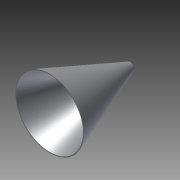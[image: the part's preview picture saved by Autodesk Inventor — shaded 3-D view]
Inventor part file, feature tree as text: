
AUTODESK INVENTOR PART (.ipt)
format: ipt  version: 2012 (Build 160160000, 160)  size: 94,208 bytes
history: native  units: in
note: dims shown in document units (in); Inventor stores cm internally (conversion verified against a paired STEP export)
features: sketch x2, plane x2, loft x1, shell x1
ambient origin geometry x8: Origin, YZ Plane, XZ Plane, XY Plane, X Axis, Y Axis, Z Axis, Center Point
feature tree (6):
  sketch  "Sketch1"  dims[d0=1.0in d1=10.0in d8=15.0in d9=8.5in]
  plane  "Work Plane1"
  plane  "Work Plane2"
  loft  "Loft2"
  shell  "Shell2"  Thickness=8.5in
  sketch  "Sketch3"  dims[d10=0.0in d11=90.0deg d12=0.0in d13=90.0deg d14=0.1in]
